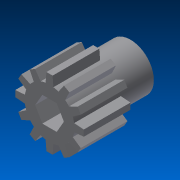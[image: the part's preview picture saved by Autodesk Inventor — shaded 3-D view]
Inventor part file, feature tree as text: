
AUTODESK INVENTOR PART (.ipt)
format: ipt  version: 2015 SP1 (Build 190203100, 203)  size: 206,848 bytes
history: native  units: in
note: dims shown in document units (in); Inventor stores cm internally (conversion verified against a paired STEP export)
features: extrude x4, sketch x4, projected_geometry x1
ambient origin geometry x8: Origin, YZ Plane, XZ Plane, XY Plane, X Axis, Y Axis, Z Axis, Center Point
bodies: Solid1 (feature_tree)
feature tree (9):
  extrude  "Extrusion1"  Depth=1.625in TaperAngle=0.0deg
  extrude  "Extrusion2"  Depth=0.9375in TaperAngle=0.0deg
  extrude  "Extrusion3"  Depth=0.5in
  extrude  "Extrusion4"  TaperAngle=120.0deg  [1 undecoded]
  sketch  "Sketch1"  dims[d0=0.9375in d1=1.625in d2=0.0in]
  sketch  "Sketch2"  dims[d3=1.0in d4=0.9375in d5=0.0in]
  sketch  "Sketch3"  dims[d6=0.5in d7=0.5in]
  sketch  "Sketch4"  dims[d8=0.5in d9=120.0deg d10=120.0deg d11=0.25in d12=0.25in d13=0.25in d14=2.0in d15=0.0in d16=0.5in d17=0.0in d18=0.1875in d19=90.0deg d20=0.5566in d21=0.6803in d22=0.0312in d23=0.0in d24=0.0625in d25=180.0deg d26=4.7244in d28=360.0deg d30=0.9375in d31=0.0in]
  projected_geometry  "Projected Loop1"
note: 1 required parameter value undecoded (feature->parameter linkage not recoverable at this tier; creation-order binding heuristic only, values carry confidence <= 0.55)
